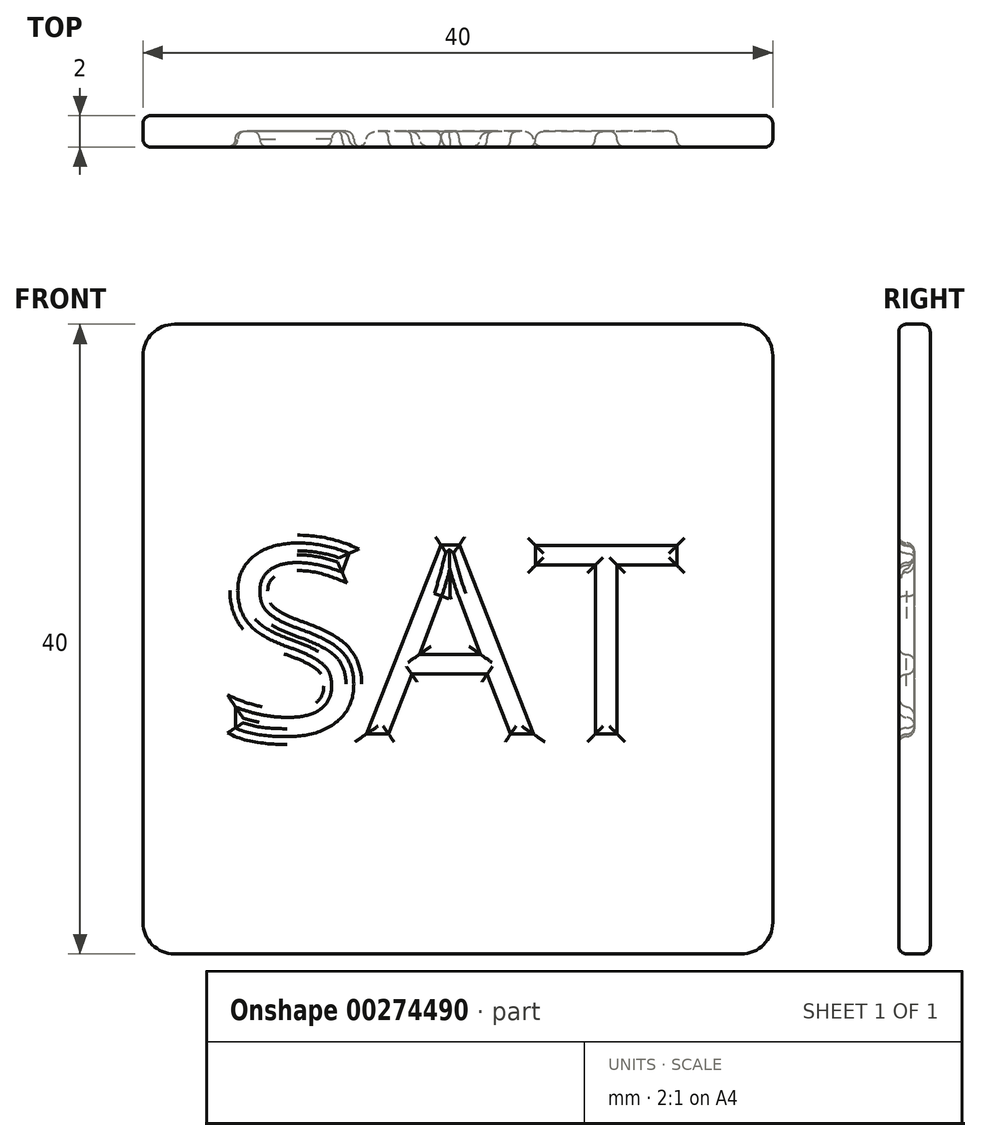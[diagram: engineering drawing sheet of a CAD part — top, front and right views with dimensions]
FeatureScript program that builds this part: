
annotation { "Feature Type Name" : "Feature", "Feature Type Description" : "" }
export const myFeature = defineFeature(function(context is Context, id is Id, definition is map)
    precondition{}
    {
        {
            var Q0;
            Q0=qCreatedBy(makeId("Front.planeOp"),FACE);
            var sketch = newSketch(context, id + "F0", { "sketchPlane" : qUnion([Q0])});
            skLineSegment(sketch, "E0.bottom", {"start": v(18, -20) * mm, "end": v(-18, -20) * mm});
            skLineSegment(sketch, "E0.top", {"start": v(18, 20) * mm, "end": v(-18, 20) * mm});
            skLineSegment(sketch, "E0.left", {"start": v(20, -18) * mm, "end": v(20, 18) * mm});
            skLineSegment(sketch, "E0.right", {"start": v(-20, -18) * mm, "end": v(-20, 18) * mm});
            skPoint(sketch, "E0.middle", {"position": v(0, 0) * mm});
            skPoint(sketch, "E1.visualSharp", {"position": v(-20, 20) * mm});
            skArc(sketch, "E1.filletArc", {"start": v(-18, 20) * mm, "mid": v(-19.41, 19.41) * mm, "end": v(-20, 18) * mm});
            skPoint(sketch, "E2.visualSharp", {"position": v(20, 20) * mm});
            skArc(sketch, "E2.filletArc", {"start": v(20, 18) * mm, "mid": v(19.41, 19.41) * mm, "end": v(18, 20) * mm});
            skPoint(sketch, "E3.visualSharp", {"position": v(20, -20) * mm});
            skArc(sketch, "E3.filletArc", {"start": v(18, -20) * mm, "mid": v(19.41, -19.41) * mm, "end": v(20, -18) * mm});
            skPoint(sketch, "E4.visualSharp", {"position": v(-20, -20) * mm});
            skArc(sketch, "E4.filletArc", {"start": v(-20, -18) * mm, "mid": v(-19.41, -19.41) * mm, "end": v(-18, -20) * mm});
            skSolve(sketch);
        }
        {
            var Q0;
            Q0=makeQuery(id+"F0.imprint","IMPRINT",FACE,{"disambiguationData":[TD([[makeQuery(id+"F0.imprint","IMPRINT",EDGE,{"derivedFrom":sQuery(id+"F0.wireOp",EDGE,"E0.bottom")}),-1.0]])]});
            extrude(context, id + "F1", {"entities" : qUnion([Q0]), "depth" : 2 * mm});
        }
        {
            var Q0;
            Q0=makeQuery(id+"F1.opExtrude","CAP_FACE",FACE,{"disambiguationData":[OSD([sQuery(id+"F0.wireOp",EDGE,"E0.bottom"),sQuery(id+"F0.wireOp",EDGE,"E0.top"),sQuery(id+"F0.wireOp",EDGE,"E0.left"),sQuery(id+"F0.wireOp",EDGE,"E0.right"),sQuery(id+"F0.wireOp",EDGE,"E1.filletArc"),sQuery(id+"F0.wireOp",EDGE,"E2.filletArc"),sQuery(id+"F0.wireOp",EDGE,"E3.filletArc"),sQuery(id+"F0.wireOp",EDGE,"E4.filletArc")])],"isStart":false});
            var sketch = newSketch(context, id + "F2", { "sketchPlane" : qUnion([Q0])});
            skText(sketch, "E5", { "text": "SAT", "fontName": "OpenSans-Regular.ttf"});
            const initialGuessF2  = {"E5": [-0.015, -0.00603, 1, 0, 0.01206]};
            skSetInitialGuess(sketch, initialGuessF2);
            skSolve(sketch);
        }
        {
            var Q0;
            Q0 = qSketchRegion(id + "F2", true);
            extrude(context, id + "F3", {"entities" : qUnion([Q0]), "operationType" : NewBodyOperationType.REMOVE, "oppositeDirection" : true, "depth" : 1 * mm});
        }
        {
            var Q0;
            Q0=makeQuery(id+"F3.boolean.opBoolean","COPY",FACE,{"derivedFrom":makeQuery(id+"F3.opExtrude","CAP_FACE",FACE,{"disambiguationData":[OSD([sQuery(id+"F2.wireOp",EDGE,"E5.sketch_text.stroke-0"),sQuery(id+"F2.wireOp",EDGE,"E5.sketch_text.stroke-1"),sQuery(id+"F2.wireOp",EDGE,"E5.sketch_text.stroke-2"),sQuery(id+"F2.wireOp",EDGE,"E5.sketch_text.stroke-3"),sQuery(id+"F2.wireOp",EDGE,"E5.sketch_text.stroke-4"),sQuery(id+"F2.wireOp",EDGE,"E5.sketch_text.stroke-5"),sQuery(id+"F2.wireOp",EDGE,"E5.sketch_text.stroke-6"),sQuery(id+"F2.wireOp",EDGE,"E5.sketch_text.stroke-7"),sQuery(id+"F2.wireOp",EDGE,"E5.sketch_text.stroke-8"),sQuery(id+"F2.wireOp",EDGE,"E5.sketch_text.stroke-9"),sQuery(id+"F2.wireOp",EDGE,"E5.sketch_text.stroke-10"),sQuery(id+"F2.wireOp",EDGE,"E5.sketch_text.stroke-11"),sQuery(id+"F2.wireOp",EDGE,"E5.sketch_text.stroke-12"),sQuery(id+"F2.wireOp",EDGE,"E5.sketch_text.stroke-13"),sQuery(id+"F2.wireOp",EDGE,"E5.sketch_text.stroke-14"),sQuery(id+"F2.wireOp",EDGE,"E5.sketch_text.stroke-15"),sQuery(id+"F2.wireOp",EDGE,"E5.sketch_text.stroke-16"),sQuery(id+"F2.wireOp",EDGE,"E5.sketch_text.stroke-17"),sQuery(id+"F2.wireOp",EDGE,"E5.sketch_text.stroke-18"),sQuery(id+"F2.wireOp",EDGE,"E5.sketch_text.stroke-19"),sQuery(id+"F2.wireOp",EDGE,"E5.sketch_text.stroke-20"),sQuery(id+"F2.wireOp",EDGE,"E5.sketch_text.stroke-21"),sQuery(id+"F2.wireOp",EDGE,"E5.sketch_text.stroke-22"),sQuery(id+"F2.wireOp",EDGE,"E5.sketch_text.stroke-23"),sQuery(id+"F2.wireOp",EDGE,"E5.sketch_text.stroke-24")])],"isStart":false})});
            var Q1;
            Q1=makeQuery(id+"F3.boolean.opBoolean","COPY",FACE,{"derivedFrom":makeQuery(id+"F3.opExtrude","CAP_FACE",FACE,{"disambiguationData":[OSD([sQuery(id+"F2.wireOp",EDGE,"E5.sketch_text.stroke-25"),sQuery(id+"F2.wireOp",EDGE,"E5.sketch_text.stroke-26"),sQuery(id+"F2.wireOp",EDGE,"E5.sketch_text.stroke-27"),sQuery(id+"F2.wireOp",EDGE,"E5.sketch_text.stroke-28"),sQuery(id+"F2.wireOp",EDGE,"E5.sketch_text.stroke-29"),sQuery(id+"F2.wireOp",EDGE,"E5.sketch_text.stroke-30"),sQuery(id+"F2.wireOp",EDGE,"E5.sketch_text.stroke-31"),sQuery(id+"F2.wireOp",EDGE,"E5.sketch_text.stroke-32"),sQuery(id+"F2.wireOp",EDGE,"E5.sketch_text.stroke-33"),sQuery(id+"F2.wireOp",EDGE,"E5.sketch_text.stroke-34"),sQuery(id+"F2.wireOp",EDGE,"E5.sketch_text.stroke-35"),sQuery(id+"F2.wireOp",EDGE,"E5.sketch_text.stroke-36"),sQuery(id+"F2.wireOp",EDGE,"E5.sketch_text.stroke-37")])],"isStart":false})});
            var Q2;
            Q2=makeQuery(id+"F3.boolean.opBoolean","COPY",FACE,{"derivedFrom":makeQuery(id+"F3.opExtrude","CAP_FACE",FACE,{"disambiguationData":[OSD([sQuery(id+"F2.wireOp",EDGE,"E5.sketch_text.stroke-38"),sQuery(id+"F2.wireOp",EDGE,"E5.sketch_text.stroke-39"),sQuery(id+"F2.wireOp",EDGE,"E5.sketch_text.stroke-40"),sQuery(id+"F2.wireOp",EDGE,"E5.sketch_text.stroke-41"),sQuery(id+"F2.wireOp",EDGE,"E5.sketch_text.stroke-42"),sQuery(id+"F2.wireOp",EDGE,"E5.sketch_text.stroke-43"),sQuery(id+"F2.wireOp",EDGE,"E5.sketch_text.stroke-44"),sQuery(id+"F2.wireOp",EDGE,"E5.sketch_text.stroke-45")])],"isStart":false})});
            var Q3;
            {var subQ0=sQuery(id+"F0.wireOp",EDGE,"E4.filletArc");var subQ1=sQuery(id+"F0.wireOp",EDGE,"E3.filletArc");var subQ2=sQuery(id+"F0.wireOp",EDGE,"E1.filletArc");var subQ3=sQuery(id+"F0.wireOp",EDGE,"E0.top");var subQ4=sQuery(id+"F0.wireOp",EDGE,"E0.right");var subQ5=sQuery(id+"F0.wireOp",EDGE,"E0.bottom");var subQ6=sQuery(id+"F0.wireOp",EDGE,"E2.filletArc");var subQ7=sQuery(id+"F0.wireOp",EDGE,"E0.left");Q3=makeQuery(id+"F3.boolean.opBoolean","SPLIT",FACE,{"disambiguationData":[TD([makeQuery(id+"F1.opExtrude","SWEPT_FACE",FACE,{"disambiguationData":[OSD([subQ5])]})])],"derivedFrom":makeQuery(id+"F1.opExtrude","CAP_FACE",FACE,{"disambiguationData":[OSD([subQ5,subQ3,subQ7,subQ4,subQ2,subQ6,subQ1,subQ0])],"isStart":false})});}
            var Q4;
            Q4=makeQuery(id+"F3.boolean.opBoolean","SPLIT",FACE,{"disambiguationData":[TD([makeQuery(id+"F3.opExtrude","SWEPT_FACE",FACE,{"disambiguationData":[OSD([sQuery(id+"F2.wireOp",EDGE,"E5.sketch_text.stroke-33")])]})])],"derivedFrom":makeQuery(id+"F1.opExtrude","CAP_FACE",FACE,{"disambiguationData":[OSD([sQuery(id+"F0.wireOp",EDGE,"E0.bottom"),sQuery(id+"F0.wireOp",EDGE,"E0.top"),sQuery(id+"F0.wireOp",EDGE,"E0.left"),sQuery(id+"F0.wireOp",EDGE,"E0.right"),sQuery(id+"F0.wireOp",EDGE,"E1.filletArc"),sQuery(id+"F0.wireOp",EDGE,"E2.filletArc"),sQuery(id+"F0.wireOp",EDGE,"E3.filletArc"),sQuery(id+"F0.wireOp",EDGE,"E4.filletArc")])],"isStart":false})});
            var Q5;
            Q5=makeQuery(id+"F1.opExtrude","CAP_FACE",FACE,{"disambiguationData":[OSD([sQuery(id+"F0.wireOp",EDGE,"E0.bottom"),sQuery(id+"F0.wireOp",EDGE,"E0.top"),sQuery(id+"F0.wireOp",EDGE,"E0.left"),sQuery(id+"F0.wireOp",EDGE,"E0.right"),sQuery(id+"F0.wireOp",EDGE,"E1.filletArc"),sQuery(id+"F0.wireOp",EDGE,"E2.filletArc"),sQuery(id+"F0.wireOp",EDGE,"E3.filletArc"),sQuery(id+"F0.wireOp",EDGE,"E4.filletArc")])],"isStart":true});
            fillet(context, id + "F4", {"entities" : qUnion([Q0, Q1, Q2, Q3, Q4, Q5]), "radius" : .5 * mm, "tangentPropagation" : true, "allowEdgeOverflow" : false});
        }
    });
